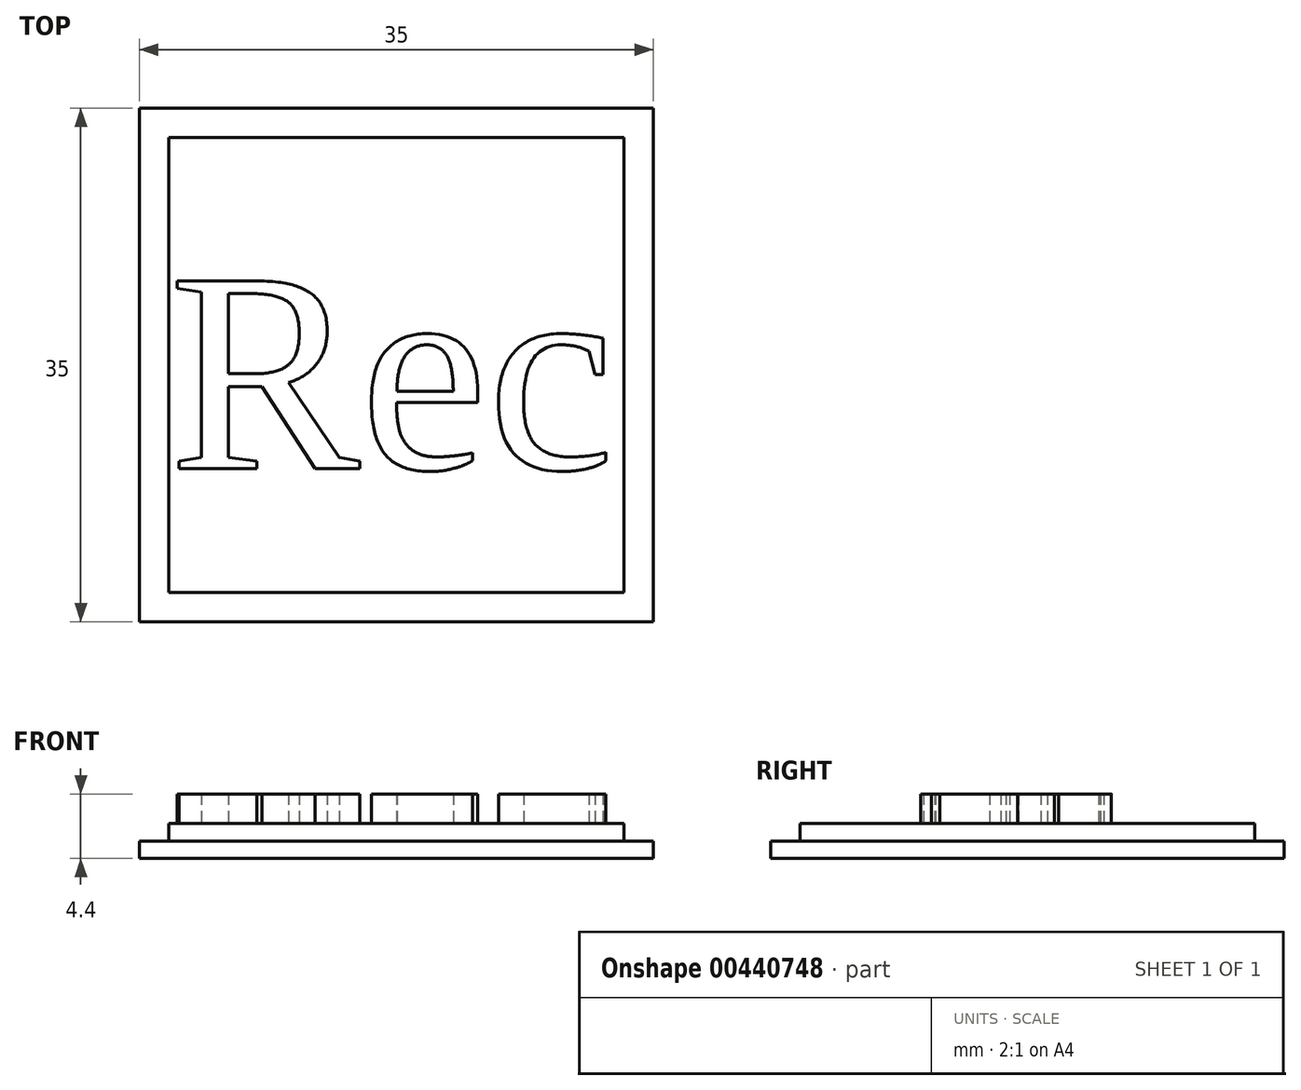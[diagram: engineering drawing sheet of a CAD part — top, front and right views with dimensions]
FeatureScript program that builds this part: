
annotation { "Feature Type Name" : "Feature", "Feature Type Description" : "" }
export const myFeature = defineFeature(function(context is Context, id is Id, definition is map)
    precondition{}
    {
        {
            var Q0;
            Q0=qCreatedBy(makeId("Top.planeOp"),FACE);
            var sketch = newSketch(context, id + "F0", { "sketchPlane" : qUnion([Q0])});
            skLineSegment(sketch, "E0.bottom", {"start": v(0, 0) * mm, "end": v(35, 0) * mm});
            skLineSegment(sketch, "E0.top", {"start": v(0, 35) * mm, "end": v(35, 35) * mm});
            skLineSegment(sketch, "E0.left", {"start": v(0, 0) * mm, "end": v(0, 35) * mm});
            skLineSegment(sketch, "E0.right", {"start": v(35, 0) * mm, "end": v(35, 35) * mm});
            skSolve(sketch);
        }
        {
            var Q0;
            Q0=qSketchRegion(id+"F0",true);
            extrude(context, id + "F1", {"entities" : qUnion([Q0]), "depth" : 1.2 * mm});
        }
        {
            var Q0;
            Q0=makeQuery(id+"F1.opExtrude","CAP_FACE",FACE,{"disambiguationData":[OSD([sQuery(id+"F0.wireOp",EDGE,"E0.bottom"),sQuery(id+"F0.wireOp",EDGE,"E0.top"),sQuery(id+"F0.wireOp",EDGE,"E0.left"),sQuery(id+"F0.wireOp",EDGE,"E0.right")])],"isStart":false});
            var sketch = newSketch(context, id + "F2", { "sketchPlane" : qUnion([Q0])});
            skLineSegment(sketch, "E1.0", {"start": v(33, 33) * mm, "end": v(2, 33) * mm});
            skLineSegment(sketch, "E1.1", {"start": v(33, 2) * mm, "end": v(33, 33) * mm});
            skLineSegment(sketch, "E1.2", {"start": v(2, 2) * mm, "end": v(33, 2) * mm});
            skLineSegment(sketch, "E1.3", {"start": v(2, 33) * mm, "end": v(2, 2) * mm});
            skSolve(sketch);
        }
        {
            var Q0;
            Q0=makeQuery(id+"F2.imprint","IMPRINT",FACE,{"disambiguationData":[TD([[makeQuery(id+"F2.imprint","IMPRINT",EDGE,{"derivedFrom":sQuery(id+"F2.wireOp",EDGE,"E1.0")}),1.0]])]});
            extrude(context, id + "F3", {"entities" : qUnion([Q0]), "operationType" : NewBodyOperationType.ADD, "depth" : 1.2 * mm});
        }
        {
            var Q0;
            Q0=makeQuery(id+"F3.opExtrude","CAP_FACE",FACE,{"disambiguationData":[OSD([sQuery(id+"F2.wireOp",EDGE,"E1.0"),sQuery(id+"F2.wireOp",EDGE,"E1.1"),sQuery(id+"F2.wireOp",EDGE,"E1.2"),sQuery(id+"F2.wireOp",EDGE,"E1.3")])],"isStart":false});
            var sketch = newSketch(context, id + "F4", { "sketchPlane" : qUnion([Q0])});
            skText(sketch, "E2", { "text": "Rec", "fontName": "Tinos-Regular.ttf"});
            const initialGuessF4  = {"E2": [0.002, 0.01043, 1, 0, 0.01407]};
            skSetInitialGuess(sketch, initialGuessF4);
            skSolve(sketch);
        }
        {
            var Q0;
            Q0=qSketchRegion(id+"F4",true);
            extrude(context, id + "F5", {"entities" : qUnion([Q0]), "operationType" : NewBodyOperationType.ADD, "depth" : 2 * mm});
        }
    });
